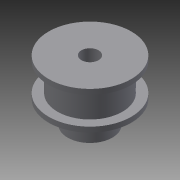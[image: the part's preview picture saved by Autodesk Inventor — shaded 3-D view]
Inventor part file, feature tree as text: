
AUTODESK INVENTOR PART (.ipt)
format: ipt  version: 2015 (Build 190159000, 159)  size: 114,176 bytes
history: native  units: mm
features: sketch x2, revolve x1, hole x1
ambient origin geometry x8: Origin, YZ Plane, XZ Plane, XY Plane, X Axis, Y Axis, Z Axis, Center Point
bodies: Solid1 (feature_tree)
feature tree (4):
  revolve  "Revolution1"  [1 undecoded]
  hole  "Hole1"  [1 undecoded]
  sketch  "Sketch1"  dims[d0=24.0mm d1=17.5mm]
  sketch  "Sketch2"  dims[d2=8.0mm d3=11.0mm d4=5.0mm d5=13.0mm d6=18.89mm d7=90.0deg d8=3.0mm d9=2.459mm d10=6.0mm d11=4.0mm d12=2.0mm d13=90.0deg d14=8.0mm d15=20.594885mm]
note: 2 required parameter values undecoded (feature->parameter linkage not recoverable at this tier; creation-order binding heuristic only, values carry confidence <= 0.55)